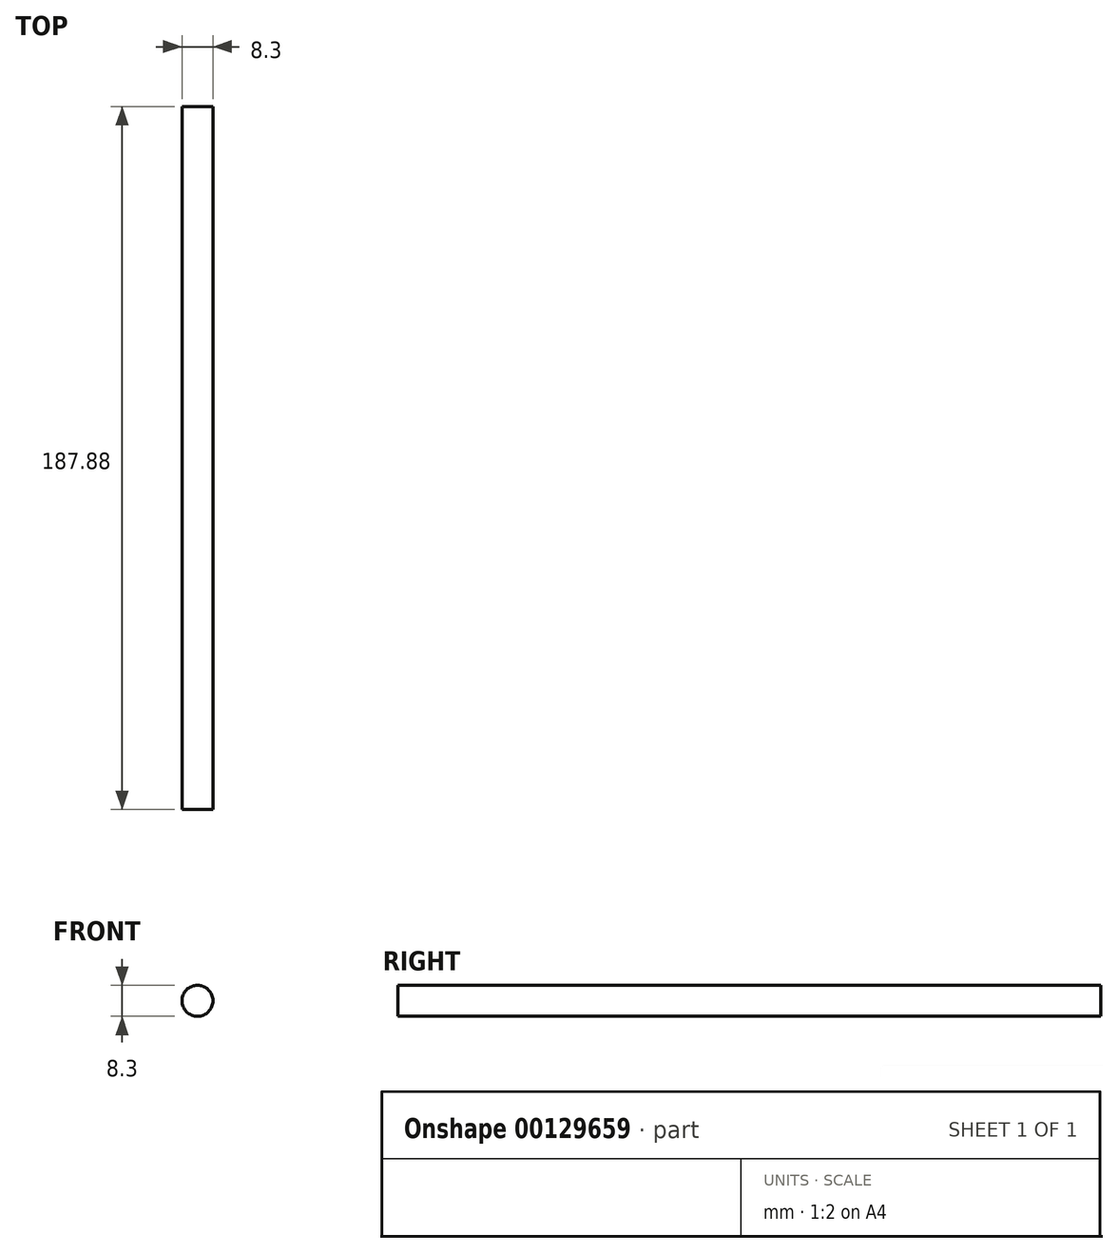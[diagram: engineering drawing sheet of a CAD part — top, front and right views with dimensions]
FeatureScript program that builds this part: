
annotation { "Feature Type Name" : "Feature", "Feature Type Description" : "" }
export const myFeature = defineFeature(function(context is Context, id is Id, definition is map)
    precondition{}
    {
        {
            var Q0;
            Q0=qCreatedBy(makeId("Front.planeOp"),FACE);
            var sketch = newSketch(context, id + "F0", { "sketchPlane" : qUnion([Q0])});
            skCircle(sketch, "E0", {"center": v(0, 0) * mm, "radius": 4.15 * mm});
            skSolve(sketch);
        }
        {
            var Q0;
            Q0=sQuery(id+"F0.wireOp",EDGE,"E0");
            extrude(context, id + "F1", {"bodyType" : ToolBodyType.SURFACE, "surfaceEntities" : qUnion([Q0]), "endBound" : BoundingType.SYMMETRIC, "depth" : 187.88 * mm});
        }
    });
